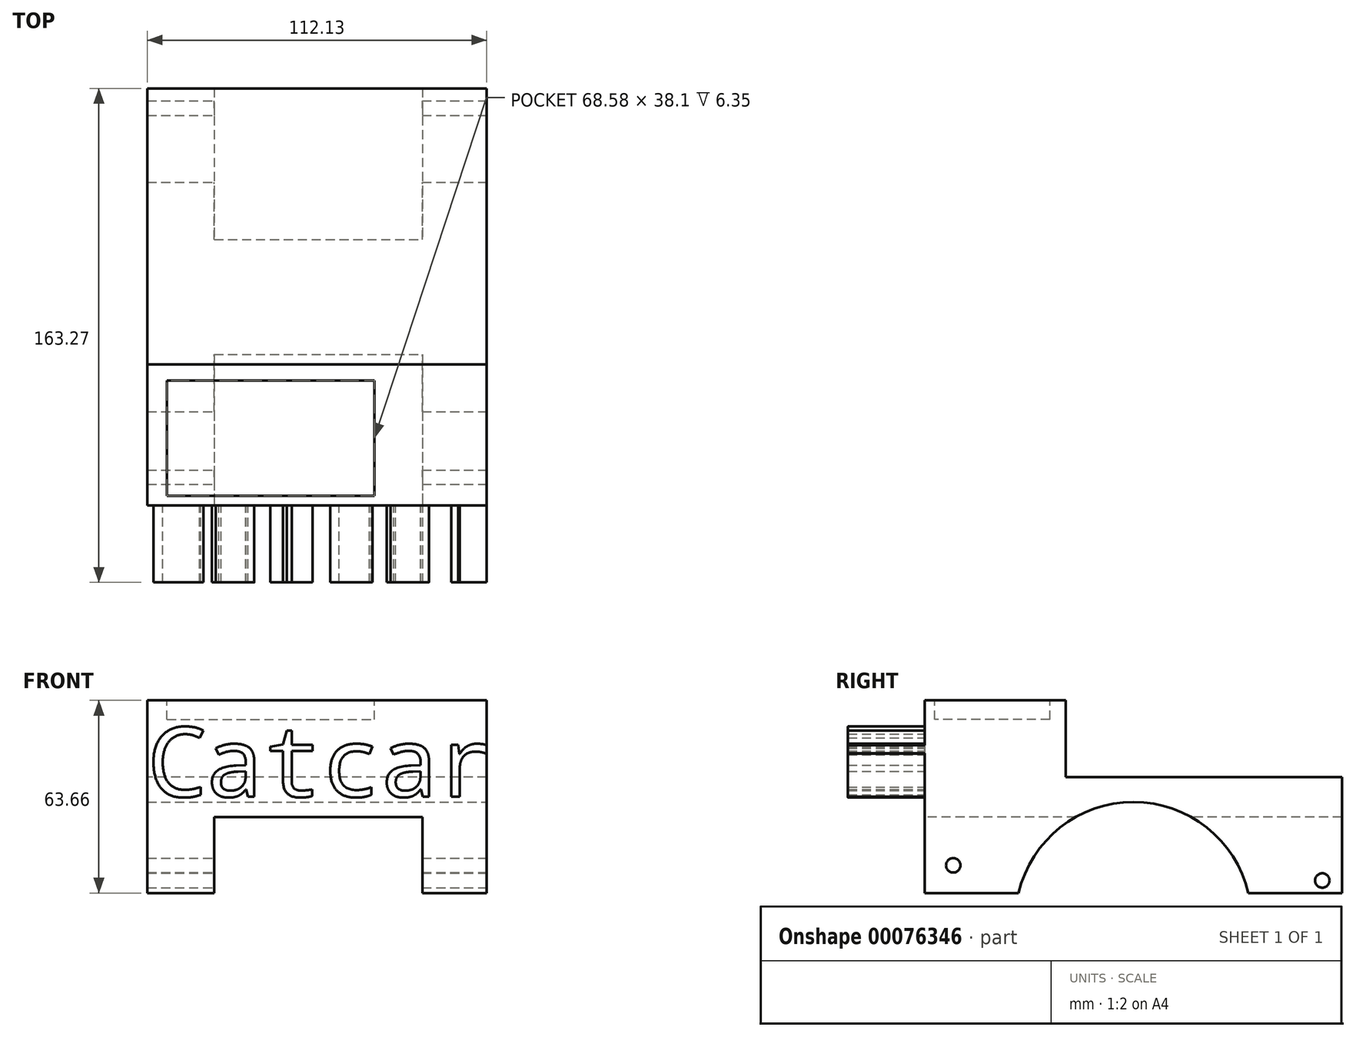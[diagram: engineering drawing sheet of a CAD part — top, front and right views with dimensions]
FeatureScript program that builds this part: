
annotation { "Feature Type Name" : "Feature", "Feature Type Description" : "" }
export const myFeature = defineFeature(function(context is Context, id is Id, definition is map)
    precondition{}
    {
        {
            var Q0;
            Q0=qCreatedBy(makeId("Front.planeOp"),FACE);
            var sketch = newSketch(context, id + "F0", { "sketchPlane" : qUnion([Q0])});
            skLineSegment(sketch, "E0.bottom", {"start": v(-57.39, 38.26) * mm, "end": v(54.74, 38.26) * mm});
            skLineSegment(sketch, "E0.top", {"start": v(-57.39, 0) * mm, "end": v(54.74, 0) * mm});
            skLineSegment(sketch, "E0.left", {"start": v(-57.39, 38.26) * mm, "end": v(-57.39, 0) * mm});
            skLineSegment(sketch, "E0.right", {"start": v(54.74, 38.26) * mm, "end": v(54.74, 0) * mm});
            skSolve(sketch);
        }
        {
            var Q0;
            Q0=makeQuery(id+"F0.imprint","IMPRINT",FACE,{"disambiguationData":[TD([[makeQuery(id+"F0.imprint","IMPRINT",EDGE,{"derivedFrom":sQuery(id+"F0.wireOp",EDGE,"E0.bottom")}),-1.0]])]});
            extrude(context, id + "F1", {"entities" : qUnion([Q0]), "depth" : 137.87 * mm});
        }
        {
            var Q0;
            Q0=makeQuery(id+"F1.opExtrude","CAP_FACE",FACE,{"disambiguationData":[OSD([sQuery(id+"F0.wireOp",EDGE,"E0.bottom"),sQuery(id+"F0.wireOp",EDGE,"E0.top"),sQuery(id+"F0.wireOp",EDGE,"E0.left"),sQuery(id+"F0.wireOp",EDGE,"E0.right")])],"isStart":false});
            var sketch = newSketch(context, id + "F2", { "sketchPlane" : qUnion([Q0])});
            skLineSegment(sketch, "E1.bottom", {"start": v(-35.27, 25.15) * mm, "end": v(33.51, 25.15) * mm});
            skLineSegment(sketch, "E1.top", {"start": v(-35.27, 0) * mm, "end": v(33.51, 0) * mm});
            skLineSegment(sketch, "E1.left", {"start": v(-35.27, 25.15) * mm, "end": v(-35.27, 0) * mm});
            skLineSegment(sketch, "E1.right", {"start": v(33.51, 25.15) * mm, "end": v(33.51, 0) * mm});
            skSolve(sketch);
        }
        {
            var Q0;
            Q0=makeQuery(id+"F2.imprint","IMPRINT",FACE,{"disambiguationData":[TD([[makeQuery(id+"F2.imprint","IMPRINT",EDGE,{"derivedFrom":sQuery(id+"F2.wireOp",EDGE,"E1.bottom")}),-1.0]])]});
            extrude(context, id + "F3", {"entities" : qUnion([Q0]), "operationType" : NewBodyOperationType.REMOVE, "endBound" : BoundingType.THROUGH_ALL, "oppositeDirection" : true, "depth" : 25.4 * mm});
        }
        {
            var Q0;
            Q0=makeQuery(id+"F1.opExtrude","SWEPT_FACE",FACE,{"disambiguationData":[OSD([sQuery(id+"F0.wireOp",EDGE,"E0.right")])]});
            var sketch = newSketch(context, id + "F4", { "sketchPlane" : qUnion([Q0])});
            skCircle(sketch, "E2", {"center": v(-128.5, 9.13) * mm, "radius": 2.38 * mm});
            skSolve(sketch);
        }
        {
            var Q0;
            Q0=makeQuery(id+"F4.imprint","IMPRINT",FACE,{"disambiguationData":[TD([[makeQuery(id+"F4.imprint","IMPRINT",EDGE,{"derivedFrom":sQuery(id+"F4.wireOp",EDGE,"E2")}),1.0]])]});
            extrude(context, id + "F5", {"entities" : qUnion([Q0]), "operationType" : NewBodyOperationType.REMOVE, "endBound" : BoundingType.THROUGH_ALL, "oppositeDirection" : true, "depth" : 25.4 * mm});
        }
        {
            var Q0;
            Q0=makeQuery(id+"F1.opExtrude","SWEPT_FACE",FACE,{"disambiguationData":[OSD([sQuery(id+"F0.wireOp",EDGE,"E0.right")])]});
            var sketch = newSketch(context, id + "F6", { "sketchPlane" : qUnion([Q0])});
            skCircle(sketch, "E3", {"center": v(-6.5, 4.13) * mm, "radius": 2.38 * mm});
            skSolve(sketch);
        }
        {
            var Q0;
            Q0=makeQuery(id+"F6.imprint","IMPRINT",FACE,{"disambiguationData":[TD([[makeQuery(id+"F6.imprint","IMPRINT",EDGE,{"derivedFrom":sQuery(id+"F6.wireOp",EDGE,"E3")}),1.0]])]});
            extrude(context, id + "F7", {"entities" : qUnion([Q0]), "operationType" : NewBodyOperationType.REMOVE, "endBound" : BoundingType.THROUGH_ALL, "oppositeDirection" : true, "depth" : 25.4 * mm});
        }
        {
            var Q0;
            Q0=makeQuery(id+"F1.opExtrude","SWEPT_FACE",FACE,{"disambiguationData":[OSD([sQuery(id+"F0.wireOp",EDGE,"E0.right")])]});
            var sketch = newSketch(context, id + "F8", { "sketchPlane" : qUnion([Q0])});
            skCircle(sketch, "E4", {"center": v(-68.94, -8.9) * mm, "radius": 39 * mm});
            skPoint(sketch, "E4.centerSnap0", {"position": v(-68.94, 0) * mm});
            skSolve(sketch);
        }
        {
            var Q0;
            {var subQ0=sQuery(id+"F8.wireOp",EDGE,"E4");var subQ1=makeQuery(id+"F1.opExtrude","SWEPT_EDGE",EDGE,{"disambiguationData":[OSD([sQuery(id+"F0.wireOp",EDGE,"E0.top"),sQuery(id+"F0.wireOp",EDGE,"E0.right")])]});var subQ2=makeQuery(id+"F8.imprint","INTERSECT",VERTEX,{"disambiguationData":[OD(0.0)],"derivedFrom":[subQ1,subQ0]});Q0=makeQuery(id+"F8.imprint","IMPRINT",FACE,{"disambiguationData":[TD([[makeQuery(id+"F8.imprint","IMPRINT",EDGE,{"disambiguationData":[TD([[subQ2,-1.0]])],"derivedFrom":subQ0}),1.0]])]});}
            extrude(context, id + "F9", {"entities" : qUnion([Q0]), "operationType" : NewBodyOperationType.REMOVE, "endBound" : BoundingType.THROUGH_ALL, "oppositeDirection" : true, "depth" : 25.4 * mm});
        }
        {
            var Q0;
            Q0=makeQuery(id+"F1.opExtrude","SWEPT_FACE",FACE,{"disambiguationData":[OSD([sQuery(id+"F0.wireOp",EDGE,"E0.bottom")])]});
            var sketch = newSketch(context, id + "F10", { "sketchPlane" : qUnion([Q0])});
            skLineSegment(sketch, "E5", {"start": v(0, -91.25) * mm, "end": v(-57.39, -91.25) * mm});
            skLineSegment(sketch, "E6", {"start": v(-57.39, -91.25) * mm, "end": v(-57.39, -137.87) * mm});
            skLineSegment(sketch, "E7", {"start": v(-57.39, -137.87) * mm, "end": v(54.74, -137.87) * mm});
            skLineSegment(sketch, "E8", {"start": v(54.74, -137.87) * mm, "end": v(54.74, -91.25) * mm});
            skLineSegment(sketch, "E9", {"start": v(54.74, -91.25) * mm, "end": v(0, -91.25) * mm});
            skSolve(sketch);
        }
        {
            var Q0;
            Q0=makeQuery(id+"F10.imprint","IMPRINT",FACE,{"disambiguationData":[TD([[makeQuery(id+"F10.imprint","IMPRINT",EDGE,{"derivedFrom":sQuery(id+"F10.wireOp",EDGE,"E5")}),1.0]])]});
            extrude(context, id + "F11", {"entities" : qUnion([Q0]), "operationType" : NewBodyOperationType.ADD, "depth" : 25.4 * mm});
        }
        {
            var Q0;
            Q0=makeQuery(id+"F11.opExtrude","CAP_FACE",FACE,{"disambiguationData":[OSD([sQuery(id+"F10.wireOp",EDGE,"E5"),sQuery(id+"F10.wireOp",EDGE,"E6"),sQuery(id+"F10.wireOp",EDGE,"E7"),sQuery(id+"F10.wireOp",EDGE,"E8"),sQuery(id+"F10.wireOp",EDGE,"E9")])],"isStart":false});
            var sketch = newSketch(context, id + "F12", { "sketchPlane" : qUnion([Q0])});
            skLineSegment(sketch, "E10.bottom", {"start": v(-50.91, -96.56) * mm, "end": v(17.67, -96.56) * mm});
            skLineSegment(sketch, "E10.top", {"start": v(-50.91, -134.66) * mm, "end": v(17.67, -134.66) * mm});
            skLineSegment(sketch, "E10.left", {"start": v(-50.91, -96.56) * mm, "end": v(-50.91, -134.66) * mm});
            skLineSegment(sketch, "E10.right", {"start": v(17.67, -96.56) * mm, "end": v(17.67, -134.66) * mm});
            skSolve(sketch);
        }
        {
            var Q0;
            Q0=makeQuery(id+"F12.imprint","IMPRINT",FACE,{"disambiguationData":[TD([[makeQuery(id+"F12.imprint","IMPRINT",EDGE,{"derivedFrom":sQuery(id+"F12.wireOp",EDGE,"E10.bottom")}),-1.0]])]});
            extrude(context, id + "F13", {"entities" : qUnion([Q0]), "operationType" : NewBodyOperationType.REMOVE, "oppositeDirection" : true, "depth" : 6.35 * mm});
        }
        {
            var Q0;
            Q0=makeQuery(id+"F11.boolean.opBoolean","MERGE",FACE,{"derivedFrom":[makeQuery(id+"F1.opExtrude","CAP_FACE",FACE,{"disambiguationData":[OSD([sQuery(id+"F0.wireOp",EDGE,"E0.bottom"),sQuery(id+"F0.wireOp",EDGE,"E0.top"),sQuery(id+"F0.wireOp",EDGE,"E0.left"),sQuery(id+"F0.wireOp",EDGE,"E0.right")])],"isStart":false}),makeQuery(id+"F11.opExtrude","SWEPT_FACE",FACE,{"disambiguationData":[OSD([sQuery(id+"F10.wireOp",EDGE,"E7")])]})]});
            var sketch = newSketch(context, id + "F14", { "sketchPlane" : qUnion([Q0])});
            skText(sketch, "E11", { "text": "Catcar", "fontName": "DroidSansMono.ttf"});
            const initialGuessF14  = {"E11": [-0.05739, 0.03183, 1, 0, 0.0231]};
            skSetInitialGuess(sketch, initialGuessF14);
            skSolve(sketch);
        }
        {
            var Q0;
            Q0=makeQuery(id+"F14.imprint","IMPRINT",FACE,{"disambiguationData":[TD([[makeQuery(id+"F14.imprint","IMPRINT",EDGE,{"derivedFrom":sQuery(id+"F14.wireOp",EDGE,"E11.sketch_text.stroke-14")}),-1.0]])]});
            var Q1;
            {var subQ0=sQuery(id+"F14.wireOp",EDGE,"E11.sketch_text.stroke-91");Q1=makeQuery(id+"F14.imprint","IMPRINT",FACE,{"disambiguationData":[TD([[makeQuery(id+"F14.imprint","IMPRINT",EDGE,{"derivedFrom":subQ0}),-1.0]])]});}
            var Q2;
            Q2=makeQuery(id+"F14.imprint","IMPRINT",FACE,{"disambiguationData":[TD([[makeQuery(id+"F14.imprint","IMPRINT",EDGE,{"derivedFrom":sQuery(id+"F14.wireOp",EDGE,"E11.sketch_text.stroke-0")}),-1.0]])]});
            var Q3;
            Q3=makeQuery(id+"F14.imprint","IMPRINT",FACE,{"disambiguationData":[TD([[makeQuery(id+"F14.imprint","IMPRINT",EDGE,{"derivedFrom":sQuery(id+"F14.wireOp",EDGE,"E11.sketch_text.stroke-66")}),-1.0]])]});
            var Q4;
            Q4=makeQuery(id+"F14.imprint","IMPRINT",FACE,{"disambiguationData":[TD([[makeQuery(id+"F14.imprint","IMPRINT",EDGE,{"derivedFrom":sQuery(id+"F14.wireOp",EDGE,"E11.sketch_text.stroke-38")}),-1.0]])]});
            var Q5;
            Q5=makeQuery(id+"F14.imprint","IMPRINT",FACE,{"disambiguationData":[TD([[makeQuery(id+"F14.imprint","IMPRINT",EDGE,{"derivedFrom":sQuery(id+"F14.wireOp",EDGE,"E11.sketch_text.stroke-54")}),-1.0]])]});
            extrude(context, id + "F15", {"entities" : qUnion([Q0, Q1, Q2, Q3, Q4, Q5]), "operationType" : NewBodyOperationType.ADD, "depth" : 25.4 * mm});
        }
    });
